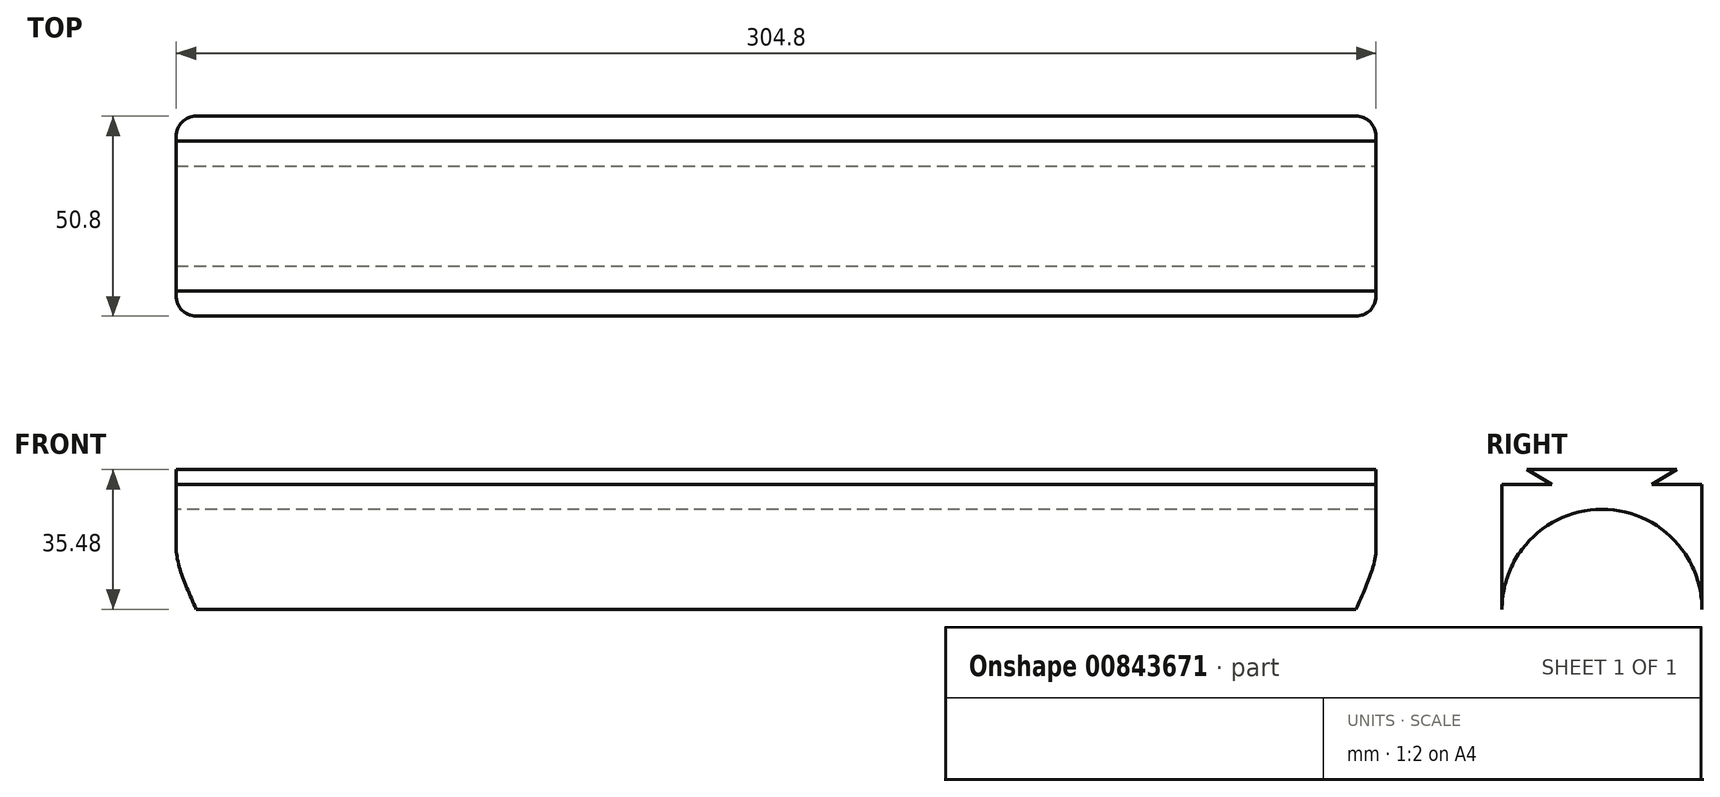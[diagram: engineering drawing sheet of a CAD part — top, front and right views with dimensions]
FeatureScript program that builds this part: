
annotation { "Feature Type Name" : "Feature", "Feature Type Description" : "" }
export const myFeature = defineFeature(function(context is Context, id is Id, definition is map)
    precondition{}
    {
        {
            var Q0;
            Q0=qCreatedBy(makeId("Top.planeOp"),FACE);
            var sketch = newSketch(context, id + "F0", { "sketchPlane" : qUnion([Q0])});
            skLineSegment(sketch, "E0.bottom", {"start": v(152.4, 25.4) * mm, "end": v(-152.4, 25.4) * mm});
            skLineSegment(sketch, "E0.top", {"start": v(152.4, -25.4) * mm, "end": v(-152.4, -25.4) * mm});
            skLineSegment(sketch, "E0.left", {"start": v(152.4, 25.4) * mm, "end": v(152.4, -25.4) * mm});
            skLineSegment(sketch, "E0.right", {"start": v(-152.4, 25.4) * mm, "end": v(-152.4, -25.4) * mm});
            skPoint(sketch, "E0.middle", {"position": v(0, 0) * mm});
            skLineSegment(sketch, "E1", {"start": v(-152.4, 25.4) * mm, "end": v(152.4, -25.4) * mm, "construction": true});
            skLineSegment(sketch, "E2", {"start": v(-152.4, -25.4) * mm, "end": v(152.4, 25.4) * mm, "construction": true});
            skSolve(sketch);
        }
        {
            var Q0;
            Q0=qSketchRegion(id+"F0",true);
            extrude(context, id + "F1", {"entities" : qUnion([Q0]), "depth" : 31.75 * mm, "offsetDistance" : 25.4 * mm});
        }
        {
            var Q0;
            Q0=makeQuery(id+"F1.opExtrude","SWEPT_EDGE",EDGE,{"disambiguationData":[OSD([sQuery(id+"F0.wireOp",EDGE,"E0.bottom"),sQuery(id+"F0.wireOp",EDGE,"E0.right")])]});
            var Q1;
            Q1=makeQuery(id+"F1.opExtrude","SWEPT_EDGE",EDGE,{"disambiguationData":[OSD([sQuery(id+"F0.wireOp",EDGE,"E0.top"),sQuery(id+"F0.wireOp",EDGE,"E0.right")])]});
            var Q2;
            Q2=makeQuery(id+"F1.opExtrude","SWEPT_EDGE",EDGE,{"disambiguationData":[OSD([sQuery(id+"F0.wireOp",EDGE,"E0.bottom"),sQuery(id+"F0.wireOp",EDGE,"E0.left")])]});
            var Q3;
            Q3=makeQuery(id+"F1.opExtrude","SWEPT_EDGE",EDGE,{"disambiguationData":[OSD([sQuery(id+"F0.wireOp",EDGE,"E0.top"),sQuery(id+"F0.wireOp",EDGE,"E0.left")])]});
            fillet(context, id + "F2", {"entities" : qUnion([Q0, Q1, Q2, Q3]), "radius" : 5.08 * mm, "tangentPropagation" : true, "allowEdgeOverflow" : false});
        }
        {
            var Q0;
            Q0=makeQuery(id+"F1.opExtrude","SWEPT_FACE",FACE,{"disambiguationData":[OSD([sQuery(id+"F0.wireOp",EDGE,"E0.right")])]});
            var sketch = newSketch(context, id + "F3", { "sketchPlane" : qUnion([Q0])});
            skArc(sketch, "E3", {"start": v(25.4, 0) * mm, "mid": v(0, 25.4) * mm, "end": v(-25.4, 0) * mm});
            skLineSegment(sketch, "E4", {"start": v(-25.4, 0) * mm, "end": v(25.4, 0) * mm});
            skSolve(sketch);
        }
        {
            var Q0;
            Q0=qSketchRegion(id+"F3",true);
            extrude(context, id + "F4", {"entities" : qUnion([Q0]), "operationType" : NewBodyOperationType.REMOVE, "endBound" : BoundingType.THROUGH_ALL, "oppositeDirection" : true, "depth" : 25.4 * mm, "offsetDistance" : 25.4 * mm});
        }
        {
            var Q0;
            Q0=makeQuery(id+"F1.opExtrude","SWEPT_FACE",FACE,{"disambiguationData":[OSD([sQuery(id+"F0.wireOp",EDGE,"E0.left")])]});
            var sketch = newSketch(context, id + "F5", { "sketchPlane" : qUnion([Q0])});
            skLineSegment(sketch, "E5", {"start": v(0, 31.75) * mm, "end": v(-12.7, 31.75) * mm});
            skLineSegment(sketch, "E6", {"start": v(-12.7, 31.75) * mm, "end": v(-19.05, 35.48) * mm});
            skLineSegment(sketch, "E7", {"start": v(-19.05, 35.48) * mm, "end": v(19.05, 35.48) * mm});
            skLineSegment(sketch, "E8", {"start": v(19.05, 35.48) * mm, "end": v(12.7, 31.75) * mm});
            skLineSegment(sketch, "E9", {"start": v(12.7, 31.75) * mm, "end": v(0, 31.75) * mm});
            skSolve(sketch);
        }
        {
            var Q0;
            Q0=makeQuery(id+"F5.imprint","IMPRINT",FACE,{"disambiguationData":[TD([[makeQuery(id+"F5.imprint","IMPRINT",EDGE,{"derivedFrom":sQuery(id+"F5.wireOp",EDGE,"E5")}),-1.0]])]});
            var Q1;
            Q1=makeQuery(id+"F1.opExtrude","SWEPT_FACE",FACE,{"disambiguationData":[OSD([sQuery(id+"F0.wireOp",EDGE,"E0.right")])]});
            extrude(context, id + "F6", {"entities" : qUnion([Q0]), "operationType" : NewBodyOperationType.ADD, "endBound" : BoundingType.UP_TO_SURFACE, "oppositeDirection" : true, "depth" : 25.4 * mm, "endBoundEntityFace" : qUnion([Q1]), "offsetDistance" : 25.4 * mm});
        }
    });
